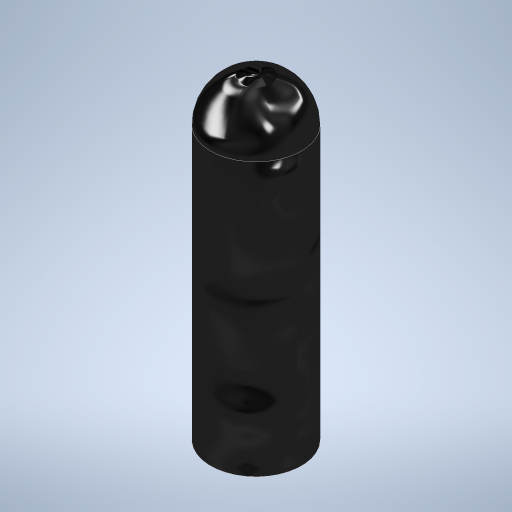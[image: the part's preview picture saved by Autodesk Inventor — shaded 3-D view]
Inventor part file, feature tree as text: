
AUTODESK INVENTOR PART (.ipt)
format: ipt  version: 2024 (Build 280153000, 153)  size: 253,952 bytes
history: native  units: mm
features: revolve x1, sketch x1
ambient origin geometry x8: Origin, YZ Plane, XZ Plane, XY Plane, X Axis, Y Axis, Z Axis, Center Point
bodies: Volumenkörper1 (feature_tree)
feature tree (2):
  revolve  "Umdrehung1"
  sketch  "Skizze1"  dims[d0=10.0mm d2=30.0mm d3=90.0deg]
